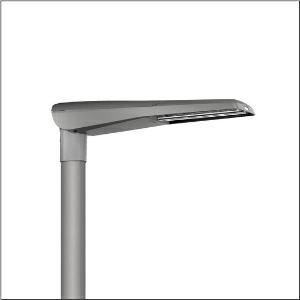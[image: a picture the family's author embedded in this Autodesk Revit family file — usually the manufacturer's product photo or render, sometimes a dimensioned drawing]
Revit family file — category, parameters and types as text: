
# Revit family: streetlight_sl_11_iq_mini___st1_0ab_5xc2nc1f08he_e776
name_source: partatom
category: Lighting Fixtures
units: mm (PartAtom-declared; Revit-internal decimal feet)

## family parameters
Cut with Voids When Loaded = No
Host = Face
Light Source = No
Part Type = Normal
Room Calculation Point = No
Round Connector Dimension = Use Diameter
Shared = No

## types (1)
- --- (1 x LED, 5460 lm, 63.6 W, 2200K)
    Apparent Load = 64 VA
    CIE Flux Codes = 29 63 95 100 100
    Color Rendering = 70
    Color Temperature = 2200K
    Default Elevation = 1800 mm
    Description = Streetlight SL 11 iQ mini, mast luminaire, primary light control with 3 zone facetted reflector, of plastic, silver coated, highly specular, primary optical cover: cover, of PMMA, transparent, light distribution: ST1.0aB, light emission: direct distribution, primary light characteristic: asymmetric, installation type: post-top, side-entry, lamps: LED, High Power LED, rated values: 6.670lm | 62,2W | 107,2lm/W (begin service life); end service life: 6.670lm | 65,6W; at 50% lumin. flux: 3.335lm | 29,4W | 113,4lm/W, colour temperature: 2200/2700/3000/4000K, colour rendering: CRI > 70, light colour: 722/727/730/740, light setting 1 begin service life: 100% | 6.670lm | 62,2W | 107,2lm/W | 3.000K, light setting 1 end service life: 65,6W, further light settings possible, control: Street-Remote, Auto-Match, Temp-Guard, Lumen-Switch, Night-Set, Smart-Wire, Light-Fading, Desk-Remote (wireless, voltage-free reading and setting of iQ features in the workshop via application-optimized NFC function/RFID function), optimised constant luminous flux control (CLO 2.0), with cable H07RN-F 5x 1.5mm², mains connection: 230..240V, AC, 50/60Hz, connection cable pre-assembled, cable length: 8,5m, luminaire housing, of diecast aluminium, powder-coated, Siteco® metallic grey (DB 702S), please order mast flange separately, inclination adjustable without tools: 0°, 5°, 10°, 15° (post-top) | 0°, -5°, -10°, -15° (side-entry), sealing non-destructively replaceable, multi-level sealing system, length: 736mm, width: 174mm, height: 116mm, mast flange for spigot size: 42mm (side-entry): 5XC10008XM4, 60/48mm (side-entry/post-top): 5XC10108XM2, 76/60mm (side-entry/post-top): 5XC10108XM1, equipment: Power, protection rating (complete): IP66, insulation class (complete): insulation class II (safety insulation), certification: CE, ENEC, ENEC+, VDE, impact resistance: IK10, permissible operating ambient temperature for outdoor applications: -25..+50°C, standard-compliant lighting for roads and squares, Environmental Product Declaration (EPD) tested and certified by an independent institute, packaging unit: 1 piece

Light Distribution: ST1.0aB
    Height = 116 mm
    Lamp = 1 x LED
    Lamp Light Flux = 5460 lm
    Lamp Power = 63.6 W
    Lamp count = 1
    Length = 736 mm
    Luminous efficacy = 86 lm/W
    Manufacturer = Siteco
    ModVariant = No
    Model = 5XC2NC1F08HE
    Number of Poles = 1
    OnlyDefault = Yes
    Power Factor = 1
    Product Name = Streetlight SL 11 iQ mini | ST1.0aB
    Product group = mast luminaire | pylon top
    ProductGroupID = 6100
    Protection Class = Protection class II
    Protection Degree = IP 66
    RLX_Detail_Level = 1
    RLX_Emergency_Light_Flux = 0 lm
    RLX_Emergency_Type = 0
    RLX_Emergency_Type_DB = No
    RlxData = <blob elided: 53033 chars, md5=7273c514>
    Socket = socket
    Standby Power = 0 W
    System Light Flux = 5460 lm
    System Power = 64 W
    Type Comments = individual setting: luminous flux: 100 % | dim-lin: 254 | 866 mA
    Type Image = l_1003508.jpg
    URL = http://relux.com
    VarID = @adj_020503
    Voltage = 0 V
    Weight = 0.00 kg
    Width = 174 mm

## geometry (parser evidence)
native form markers: Blend x4, Sweep x10
no freeform markers — native parametric forms only
